# Revit family: 2093155 Accessories_Sylvania_MC2 HORIZ-CORNER_Ceiling Recessed
name_source: partatom
category: Generic Models
revit_build: Autodesk Revit 2015 (Build: 20140606_1530(x64)
units: mm (PartAtom-declared; Revit-internal decimal feet)

## types (1)
- MC2 90° HORIZ-CORNER WHT OPAL
    Assembly Code = D5020200
    Body Material = Metal_Sylvania_Mini Continuum LED_White
    Catalog Number = 2093155 MC2 90° HORIZ-CORNER WHT OPAL
    Default Elevation = 0 mm  [stored 0 ft]
    Description = LED Mini Continuum perfect homogenous light distribution with no shadows. Clean horizontal and vertical lines of light. LED Mini Continuum is based on the Golden mean or ratio and is regarded as the secret to aesthetics. LED Mini Continuum profiles supplied complete with extrusion, diffuser & LED strips order accessories separately. 3000K & 4000K colour temperature options. Extrusion profiles offer trim and trimless options
    Diffuser Material = Polycarbonate_Sylvania_Mini Continuum LED_Opal_4000K
    Height = 86 mm  [stored 0.282152 ft]
    Manufacturer = Feilo Sylvania
    Model = MC2 90° HORIZ-CORNER WHT OPAL
    Offset = 40 mm  [stored 0.131234 ft]
    Product Family = MINI CONTINUUM II ACCESSORIES
    Product Page URL = http://www.feilosylvania.com
    URL = http://www.feilosylvania.com
    Weight = 1.80 kg
    Width = 54 mm  [stored 0.177165 ft]

note: [stored X ft] marks values corroborated as IEEE doubles in the binary element streams (Revit-internal decimal feet)

## geometry (parser evidence)
native form markers: Extrusion x4, Sweep x3
no freeform markers — native parametric forms only
